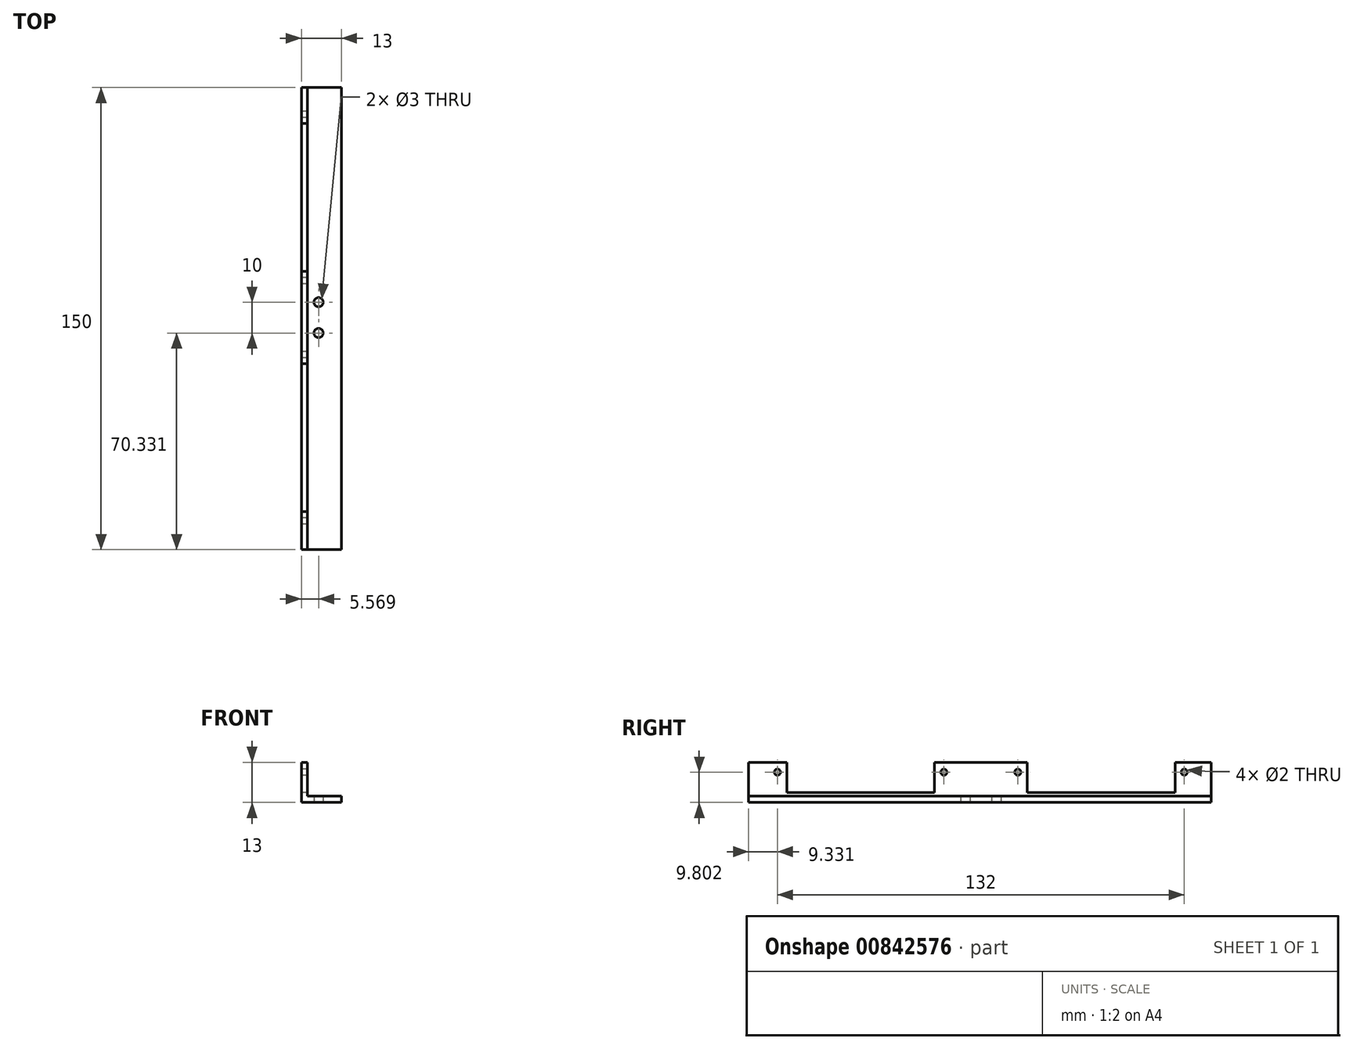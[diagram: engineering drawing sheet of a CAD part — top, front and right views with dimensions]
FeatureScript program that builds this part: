
annotation { "Feature Type Name" : "Feature", "Feature Type Description" : "" }
export const myFeature = defineFeature(function(context is Context, id is Id, definition is map)
    precondition{}
    {
        {
            var Q0;
            Q0=qCreatedBy(makeId("Front.planeOp"),FACE);
            var sketch = newSketch(context, id + "F0", { "sketchPlane" : qUnion([Q0])});
            skLineSegment(sketch, "E0", {"start": v(-33.12, 37.63) * mm, "end": v(-33.12, 24.63) * mm});
            skLineSegment(sketch, "E1", {"start": v(-33.12, 24.63) * mm, "end": v(-20.12, 24.63) * mm});
            skLineSegment(sketch, "E2", {"start": v(-33.12, 37.63) * mm, "end": v(-31.12, 37.63) * mm});
            skLineSegment(sketch, "E3", {"start": v(-20.12, 24.63) * mm, "end": v(-20.12, 26.63) * mm});
            skLineSegment(sketch, "E4", {"start": v(-31.12, 37.63) * mm, "end": v(-31.12, 26.63) * mm});
            skLineSegment(sketch, "E5", {"start": v(-20.12, 26.63) * mm, "end": v(-31.12, 26.63) * mm});
            skPoint(sketch, "E6", {"position": v(-31.12, 26.63) * mm});
            skSolve(sketch);
        }
        {
            var Q0;
            Q0 = qSketchRegion(id + "F0", true);
            extrude(context, id + "F1", {"entities" : qUnion([Q0]), "depth" : 150 * mm, "offsetDistance" : 25 * mm});
        }
        {
            var Q0;
            Q0=makeQuery(id+"F1.opExtrude","SWEPT_FACE",FACE,{"disambiguationData":[OSD([sQuery(id+"F0.wireOp",EDGE,"E1")])]});
            var sketch = newSketch(context, id + "F2", { "sketchPlane" : qUnion([Q0])});
            skPoint(sketch, "E7", {"position": v(-27.55, 69.67) * mm});
            skPoint(sketch, "E8", {"position": v(-27.55, 79.67) * mm});
            skSolve(sketch);
        }
        {
            var Q0;
            Q0=sQuery(id+"F2.wireOp",VERTEX,"E7");
            var Q1;
            Q1=sQuery(id+"F2.wireOp",VERTEX,"E8");
            var Q2;
            Q2=makeQuery(id+"F1.opExtrude","SWEPT_BODY",BODY,{"disambiguationData":[OSD([sQuery(id+"F0.wireOp",EDGE,"E0"),sQuery(id+"F0.wireOp",EDGE,"E1"),sQuery(id+"F0.wireOp",EDGE,"E2"),sQuery(id+"F0.wireOp",EDGE,"E3"),sQuery(id+"F0.wireOp",EDGE,"E4"),sQuery(id+"F0.wireOp",EDGE,"E5")])]});
            hole(context, id + "F3", {"style" : HoleStyle.SIMPLE, "endStyle" : HoleEndStyle.THROUGH, "holeDiameter" : 3 * mm, "majorDiameter" : 5 * mm, "isTappedThrough" : true, "tappedDepth" : 12 * mm, "tapClearance" : 3, "locations" : qUnion([Q0, Q1]), "scope" : qUnion([Q2])});
        }
        {
            var Q0;
            Q0=makeQuery(id+"F1.opExtrude","SWEPT_FACE",FACE,{"disambiguationData":[OSD([sQuery(id+"F0.wireOp",EDGE,"E0")])]});
            var sketch = newSketch(context, id + "F4", { "sketchPlane" : qUnion([Q0])});
            skLineSegment(sketch, "E9.bottom", {"start": v(11.67, 37.63) * mm, "end": v(59.67, 37.63) * mm});
            skLineSegment(sketch, "E9.top", {"start": v(11.67, 27.85) * mm, "end": v(59.67, 27.85) * mm});
            skLineSegment(sketch, "E9.left", {"start": v(11.67, 37.63) * mm, "end": v(11.67, 27.85) * mm});
            skLineSegment(sketch, "E9.right", {"start": v(59.67, 37.63) * mm, "end": v(59.67, 27.85) * mm});
            skLineSegment(sketch, "E10.bottom", {"start": v(89.67, 37.63) * mm, "end": v(137.67, 37.63) * mm});
            skLineSegment(sketch, "E10.top", {"start": v(89.67, 27.85) * mm, "end": v(137.67, 27.85) * mm});
            skLineSegment(sketch, "E10.left", {"start": v(89.67, 37.63) * mm, "end": v(89.67, 27.85) * mm});
            skLineSegment(sketch, "E10.right", {"start": v(137.67, 37.63) * mm, "end": v(137.67, 27.85) * mm});
            skPoint(sketch, "E11", {"position": v(8.67, 34.43) * mm});
            skLineSegment(sketch, "E12", {"start": v(0, 34.43) * mm, "end": v(150, 34.43) * mm});
            skPoint(sketch, "E13", {"position": v(62.67, 34.43) * mm});
            skPoint(sketch, "E14", {"position": v(86.67, 34.43) * mm});
            skPoint(sketch, "E15", {"position": v(11.67, 34.43) * mm});
            skPoint(sketch, "E16", {"position": v(59.67, 34.43) * mm});
            skPoint(sketch, "E17", {"position": v(89.67, 34.43) * mm});
            skPoint(sketch, "E18", {"position": v(137.67, 34.43) * mm});
            skPoint(sketch, "E19", {"position": v(140.67, 34.43) * mm});
            skSolve(sketch);
        }
        {
            var Q0;
            {var subQ0=sQuery(id+"F4.wireOp",EDGE,"E9.top");Q0=makeQuery(id+"F4.imprint","IMPRINT",FACE,{"disambiguationData":[TD([[makeQuery(id+"F4.imprint","IMPRINT",EDGE,{"derivedFrom":subQ0}),1.0]])]});}
            var Q1;
            {var subQ0=sQuery(id+"F4.wireOp",EDGE,"E9.bottom");Q1=makeQuery(id+"F4.imprint","IMPRINT",FACE,{"disambiguationData":[TD([[makeQuery(id+"F4.imprint","IMPRINT",EDGE,{"derivedFrom":subQ0}),1.0]])]});}
            var Q2;
            {var subQ0=sQuery(id+"F4.wireOp",EDGE,"E10.bottom");Q2=makeQuery(id+"F4.imprint","IMPRINT",FACE,{"disambiguationData":[TD([[makeQuery(id+"F4.imprint","IMPRINT",EDGE,{"derivedFrom":subQ0}),1.0]])]});}
            var Q3;
            {var subQ0=sQuery(id+"F4.wireOp",EDGE,"E10.top");Q3=makeQuery(id+"F4.imprint","IMPRINT",FACE,{"disambiguationData":[TD([[makeQuery(id+"F4.imprint","IMPRINT",EDGE,{"derivedFrom":subQ0}),1.0]])]});}
            extrude(context, id + "F5", {"entities" : qUnion([Q0, Q1, Q2, Q3]), "operationType" : NewBodyOperationType.REMOVE, "oppositeDirection" : true, "depth" : 78 * mm, "offsetDistance" : 25 * mm});
        }
        {
            var Q0;
            Q0=sQuery(id+"F4.wireOp",VERTEX,"E11");
            var Q1;
            Q1=sQuery(id+"F4.wireOp",VERTEX,"E13");
            var Q2;
            Q2=sQuery(id+"F4.wireOp",VERTEX,"E14");
            var Q3;
            Q3=sQuery(id+"F4.wireOp",VERTEX,"E19");
            var Q4;
            Q4=makeQuery(id+"F1.opExtrude","SWEPT_BODY",BODY,{"disambiguationData":[OSD([sQuery(id+"F0.wireOp",EDGE,"E0"),sQuery(id+"F0.wireOp",EDGE,"E1"),sQuery(id+"F0.wireOp",EDGE,"E2"),sQuery(id+"F0.wireOp",EDGE,"E3"),sQuery(id+"F0.wireOp",EDGE,"E4"),sQuery(id+"F0.wireOp",EDGE,"E5")])]});
            hole(context, id + "F6", {"style" : HoleStyle.SIMPLE, "endStyle" : HoleEndStyle.THROUGH, "holeDiameter" : 2 * mm, "majorDiameter" : 5 * mm, "isTappedThrough" : true, "tappedDepth" : 12 * mm, "tapClearance" : 3, "locations" : qUnion([Q0, Q1, Q2, Q3]), "scope" : qUnion([Q4])});
        }
    });
